# Revit family: Camera-Security-HanwhaTechwin-Bullet-Wisenet Q-QNO-8020R_mm
name_source: partatom
category: Security Devices
units: mm (PartAtom-declared; Revit-internal decimal feet)

## family parameters
Cut with Voids When Loaded = No
Host = Face
Maintain Annotation Orientation = Yes
OmniClass Number = 23.85.30.17.14
OmniClass Title = Video Surveillance
Part Type = Normal
Room Calculation Point = No
Round Connector Dimension = Use Diameter
Shared = No

## types (1)
- Standard
    AssetType = Fixed
    Category = 5MP Network IR Bullet Camera
    Color = Dark grey
    Default Elevation = 1219.2 mm  [stored 4 ft]
    Description = NBS standard template for generic face-based components
    Features = • Max. 5Megapixel (2592 x 1944) resolution
• 2.8mm/4mm/6mm fixed lens
• 0.15Lux (Color), 0Lux (B/W, IR LED on)
• Max. 30fps@5MP (H.265 / H.264)
• H.265, H.264, MJPEG codec support, Multiple streaming
• Day & Night, WDR (120dB)
• Tampering, Motion detection, Defocus detection
• Micro SD / SDHC / SDXC memory slot (Max. 128GB)
• Hallway view, WiseStream II support
• IR Viewable length 20m/25m/30m
• IP66, IK10, PoE
    Manufacturer = Hanwha Techwin
    ManufacturerName = Hanwhatechwin
    ManufacturerURL = http://security.hanwhatechwin.com
    Material = Aluminum
    Model = QNO-8020R
    ModelNumber = QNO-8020R
    ModelReference = Hanwhatechwin
    Name = QNO-8020R
    NominalHeight = 246.0mm (9.69")
    NominalLength = Ø70.0 (Ø2.76")
    NominalWidth = Ø70.0 (Ø2.76")
    Product Documentation Link = https://www.hanwha-security.com
    Product Material = Aluminum - HanwhaTechwin - Dark grey
    Product Page URL = https://www.hanwha-security.com
    Size = Ø70.0 x 246.0mm (Ø2.76" x 9.69")
    URL = https://www.hanwha-security.com
    Uniclass2 = Pr_60_75_75_86_86
    Version = 1
    Voltage = 12 V

note: [stored X ft] marks values corroborated as IEEE doubles in the binary element streams (Revit-internal decimal feet)

## geometry (parser evidence)
native form markers: Blend x2, Sweep x6
no freeform markers — native parametric forms only
